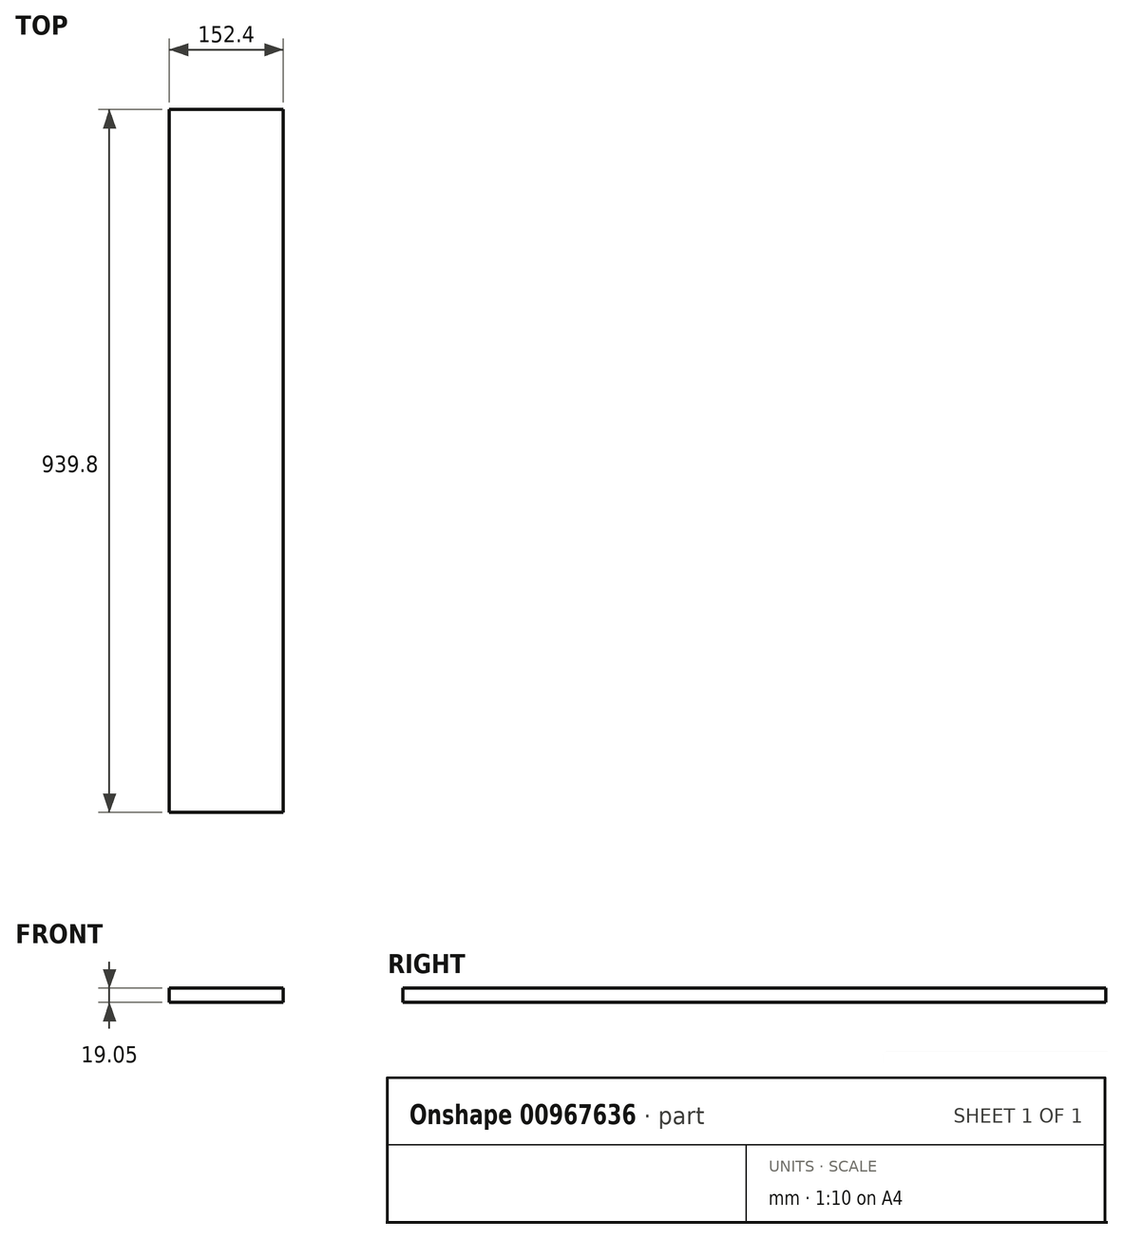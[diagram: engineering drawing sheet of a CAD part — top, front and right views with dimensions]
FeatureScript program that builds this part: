
annotation { "Feature Type Name" : "Feature", "Feature Type Description" : "" }
export const myFeature = defineFeature(function(context is Context, id is Id, definition is map)
    precondition{}
    {
        {
            var Q0;
            Q0=qCreatedBy(makeId("Top.planeOp"),FACE);
            var sketch = newSketch(context, id + "F0", { "sketchPlane" : qUnion([Q0])});
            skLineSegment(sketch, "E0.bottom", {"start": v(0, 0) * mm, "end": v(152.4, 0) * mm});
            skLineSegment(sketch, "E0.top", {"start": v(0, 939.8) * mm, "end": v(152.4, 939.8) * mm});
            skLineSegment(sketch, "E0.left", {"start": v(0, 0) * mm, "end": v(0, 939.8) * mm});
            skLineSegment(sketch, "E0.right", {"start": v(152.4, 0) * mm, "end": v(152.4, 939.8) * mm});
            skSolve(sketch);
        }
        {
            var Q0;
            Q0=makeQuery(id+"F0.imprint","IMPRINT",FACE,{"disambiguationData":[TD([[makeQuery(id+"F0.imprint","IMPRINT",EDGE,{"derivedFrom":sQuery(id+"F0.wireOp",EDGE,"E0.bottom")}),1.0]])]});
            extrude(context, id + "F1", {"entities" : qUnion([Q0]), "depth" : 19.05 * mm, "offsetDistance" : 25.4 * mm});
        }
    });
